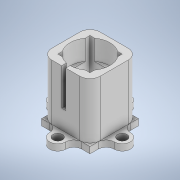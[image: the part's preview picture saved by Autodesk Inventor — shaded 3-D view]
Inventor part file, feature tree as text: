
AUTODESK INVENTOR PART (.ipt)
format: ipt  version: 2022 (Build 260153000, 153)  size: 371,712 bytes
history: native  units: in
note: dims shown in document units (in); Inventor stores cm internally (conversion verified against a paired STEP export)
features: projected_geometry x12, extrude x9, sketch x9, chamfer x2, fillet x2, thicken_offset x1
ambient origin geometry x8: Origin, YZ Plane, XZ Plane, XY Plane, X Axis, Y Axis, Z Axis, Center Point
bodies: Solid1 (feature_tree)
feature tree (35):
  extrude  "Extrusion1"  Depth=0.3986in
  extrude  "Extrusion2"  Depth=0.1in
  extrude  "Extrusion3"  Depth=0.1in
  extrude  "Extrusion4"  Depth=0.05in
  extrude  "Extrusion5"  Depth=0.0787in TaperAngle=0.0deg
  chamfer  "Chamfer4"  Distance=0.0787in
  chamfer  "Chamfer5"  Angle=90.0deg  [1 undecoded]
  extrude  "Extrusion6"  TaperAngle=90.0deg  [1 undecoded]
  fillet  "Fillet2"  Radius=0.75in
  extrude  "Extrusion7"  Depth=0.0787in TaperAngle=0.0deg
  fillet  "Fillet3"  Radius=0.125in
  extrude  "Extrusion8"  Depth=0.125in TaperAngle=45.0deg
  extrude  "Extrusion9"  Depth=0.1in
  thicken_offset  "Thicken1"
  sketch  "Sketch1"  dims[d0=0.3986in d1=0.3986in]
  sketch  "Sketch2"  dims[d2=0.1in d3=0.1in]
  projected_geometry  "Projected Loop1"
  sketch  "Sketch3"  dims[d4=0.1in d5=0.1in]
  sketch  "Sketch4"  dims[d6=0.315in d7=0.0in d8=0.05in]
  projected_geometry  "Projected Loop2"
  projected_geometry  "Projected Loop3"
  projected_geometry  "Projected Loop4"
  sketch  "Sketch5"  dims[d9=0.4331in d10=0.0in d11=0.0787in d12=0.0in]
  projected_geometry  "Projected Loop5"
  projected_geometry  "Projected Loop6"
  sketch  "Sketch6"  dims[d15=0.1in]
  projected_geometry  "Projected Loop7"
  sketch  "Sketch7"  dims[d16=0.1in]
  projected_geometry  "Projected Loop8"
  sketch  "Sketch8"  dims[d17=90.0deg]
  projected_geometry  "Projected Loop9"
  projected_geometry  "Projected Loop10"
  sketch  "Sketch9"  dims[d18=90.0deg d19=0.0787in d20=0.0in d31=90.0deg d32=90.0deg d33=0.75in d34=0.0787in d35=0.0in d36=0.1239in d37=0.125in d38=45.0deg d39=0.121in d40=0.125in d41=45.0deg d42=0.1in d43=0.2in d44=0.1in d45=0.2in d46=0.1in d47=0.1181in d48=0.1in d49=0.1181in d50=0.0787in d51=0.0in d52=0.1in d53=0.2in d54=0.1in d55=0.1in d56=0.2in d57=0.1in d58=0.1in d59=0.1181in d60=0.1181in d61=0.025in d62=0.0787in d63=0.0in d64=0.125in d65=0.4921in d66=0.1in d67=0.15in d68=0.0in d69=0.0in d70=0.1in d71=0.0in d72=0.1in d73=0.1in]
  projected_geometry  "Projected Loop11"
  projected_geometry  "Projected Loop12"
note: 2 required parameter values undecoded (feature->parameter linkage not recoverable at this tier; creation-order binding heuristic only, values carry confidence <= 0.55)
